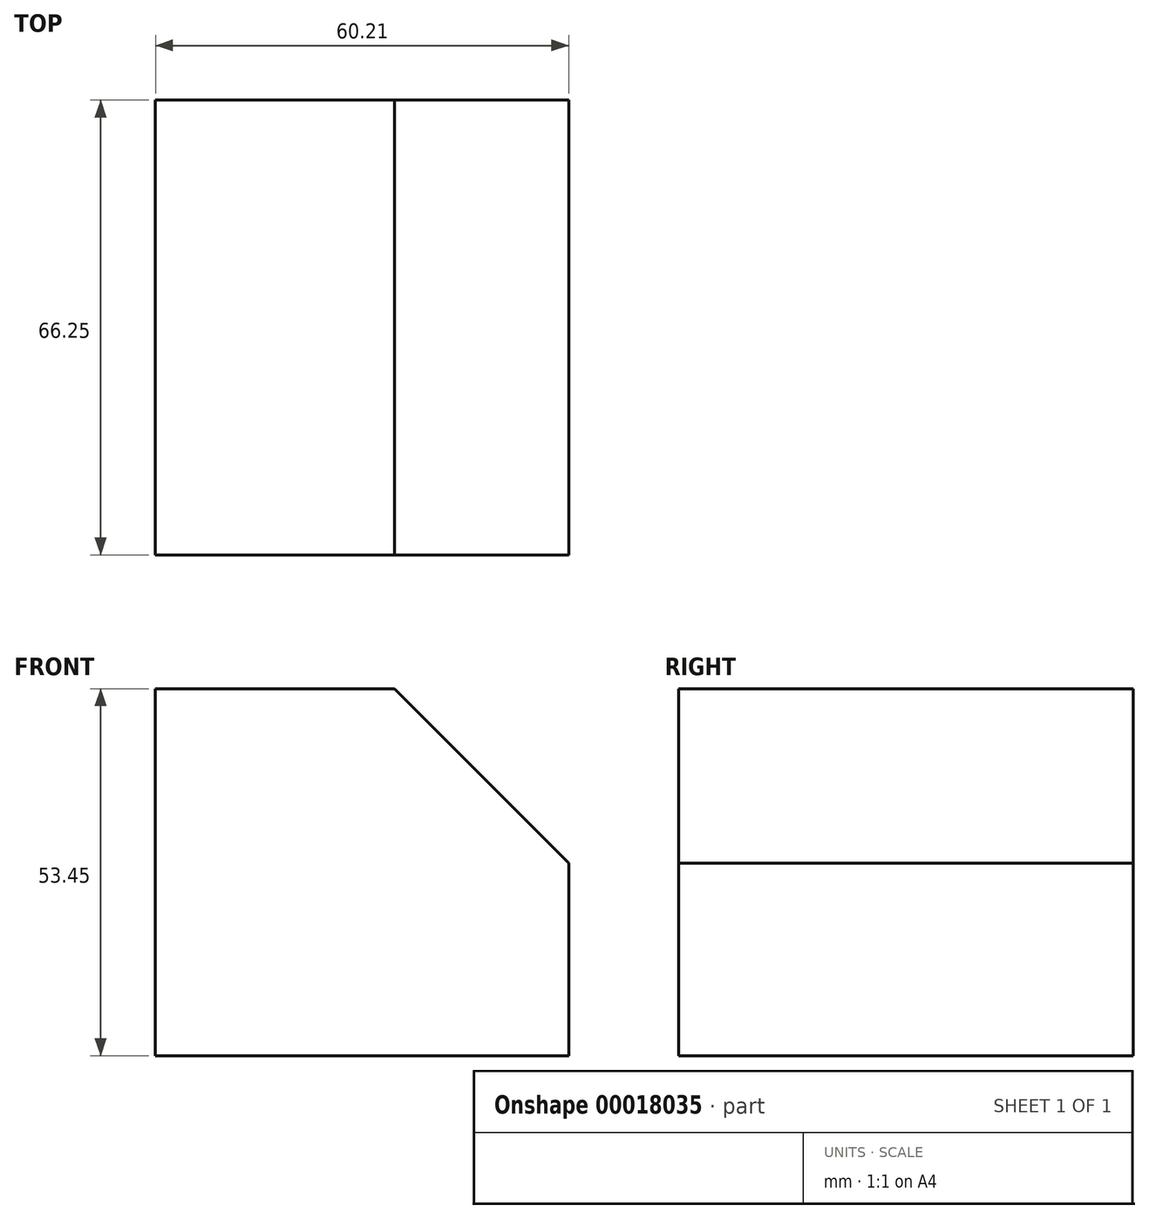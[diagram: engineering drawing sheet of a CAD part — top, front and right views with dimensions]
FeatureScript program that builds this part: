
annotation { "Feature Type Name" : "Feature", "Feature Type Description" : "" }
export const myFeature = defineFeature(function(context is Context, id is Id, definition is map)
    precondition{}
    {
        {
            var Q0;
            Q0=qCreatedBy(makeId("Front.planeOp"),FACE);
            var sketch = newSketch(context, id + "F0", { "sketchPlane" : qUnion([Q0])});
            skLineSegment(sketch, "E0.bottom", {"start": v(-29.94, 24.63) * mm, "end": v(30.27, 24.63) * mm});
            skLineSegment(sketch, "E0.top", {"start": v(-29.94, -28.82) * mm, "end": v(30.27, -28.82) * mm});
            skLineSegment(sketch, "E0.left", {"start": v(-29.94, 24.63) * mm, "end": v(-29.94, -28.82) * mm});
            skLineSegment(sketch, "E0.right", {"start": v(30.27, 24.63) * mm, "end": v(30.27, -28.82) * mm});
            skSolve(sketch);
        }
        {
            var Q0;
            Q0=makeQuery(id+"F0.imprint","IMPRINT",FACE,{"disambiguationData":[TD([[makeQuery(id+"F0.imprint","IMPRINT",EDGE,{"derivedFrom":sQuery(id+"F0.wireOp",EDGE,"E0.bottom")}),-1.0]])]});
            extrude(context, id + "F1", {"entities" : qUnion([Q0]), "depth" : 66.25 * mm});
        }
        {
            var Q0;
            Q0=makeQuery(id+"F1.opExtrude","SWEPT_EDGE",EDGE,{"disambiguationData":[OSD([sQuery(id+"F0.wireOp",EDGE,"E0.bottom"),sQuery(id+"F0.wireOp",EDGE,"E0.right")])]});
            chamfer(context, id + "F2", {"entities" : qUnion([Q0]), "width" : 25.4 * mm, "tangentPropagation" : true});
        }
    });
